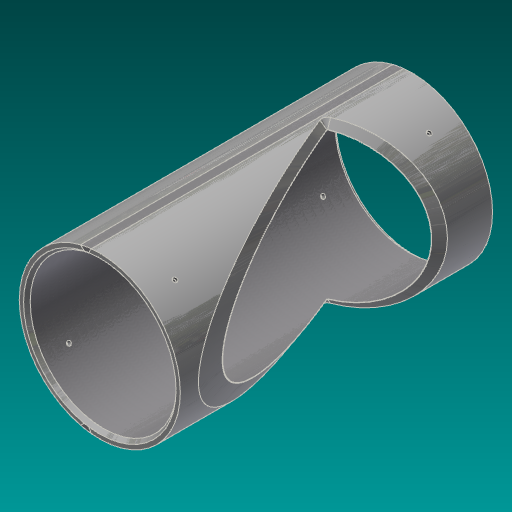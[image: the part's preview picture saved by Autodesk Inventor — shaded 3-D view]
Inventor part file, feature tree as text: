
AUTODESK INVENTOR PART (.ipt)
format: ipt  version: 2017.3 (Build 213256000, 256)  size: 478,208 bytes
history: native  units: in
note: dims shown in document units (in); Inventor stores cm internally (conversion verified against a paired STEP export)
features: other x14, extrude x8, split x8, plane x7, sketch x5, loft x4, chamfer x2, hole x2, pattern_circular x1
ambient origin geometry x8: Origin, YZ Plane, XZ Plane, XY Plane, X Axis, Y Axis, Z Axis, Center Point
bodies: Solid1 (feature_tree)
feature tree (51):
  sketch  "Sketch1"  dims[d0=30.25in d1=33.25in]
  extrude  "Extrusion1"  Depth=33.25in
  sketch  "Sketch2"  dims[d2=47.0236in d3=17.4961in d4=0.0in d5=0.0in d6=22.5deg]
  extrude  "Extrusion2"  TaperAngle=22.5deg  [1 undecoded]
  split  "Split1"
  split  "Split2"
  plane  "Work Plane1"
  plane  "Work Plane2"
  split  "Split3"
  split  "Split4"
  loft  "Loft1"
  loft  "Loft2"
  loft  "Loft3"
  loft  "Loft4"
  chamfer  "Chamfer1"  Angle=90.0deg  [1 undecoded]
  chamfer  "Chamfer2"  Angle=90.0deg  [1 undecoded]
  sketch  "Sketch3"  dims[d7=0.0938in d8=70.0in d9=0.0in]
  plane  "Work Plane3"
  plane  "Work Plane4"
  plane  "Work Plane5"
  plane  "Work Plane6"
  plane  "Work Plane7"
  hole  "Hole1"  [1 undecoded]
  hole  "Hole2"  [1 undecoded]
  pattern_circular  "Circular Pattern1"  Angle=90.0deg  [1 undecoded]
  split  "Split5"
  split  "Split6"
  split  "Split7"
  split  "Split8"
  other  "Srf1"
  other  "Srf2"
  other  "Edges1"
  other  "Edges2"
  other  "Edges3"
  other  "Edges4"
  other  "Edges5"
  other  "Edges6"
  other  "Edges7"
  other  "Edges8"
  sketch  "Sketch4"  dims[d10=30.375in d11=0.0in d12=0.0in]
  sketch  "Sketch5"  dims[d13=1.103in d14=70.0in d15=0.0in d16=22.5deg d17=22.5deg d18=0.0in d19=90.0deg d20=0.0in d21=90.0deg d22=0.0in d23=90.0deg d24=0.0in d25=90.0deg d26=0.0in d27=90.0deg d28=0.0in d29=90.0deg d30=0.0in d31=90.0deg d32=0.0in d33=90.0deg d34=0.75in d35=0.125in d36=0.2749in d37=0.75in d38=0.125in d39=0.2749in d40=75.0deg d41=0.0938in d42=0.0469in d43=0.0687in d46=0.0687in d47=135.0deg d48=-0.9276in d49=6.0in d50=6.0in d51=0.891in d52=0.553in d53=0.0246in d54=0.897in d55=0.375in d56=0.25in d57=0.5635in d58=3.0in d59=0.8108in d60=6.0in d61=6.0in d62=0.891in d63=0.553in d64=0.0246in d65=0.897in d66=0.375in d67=0.25in d68=0.5635in d69=3.0in d70=0.8108in d71=0.7874in d72=1.0994in d74=0.0in d75=0.0in d76=0.0in d77=0.0in]
  other  "Srf3"
  other  "Srf4"
  other  "Srf5"
  other  "Srf6"
  extrude  "ExtrusionSrf1"  TaperAngle=0.0deg  [1 undecoded]
  extrude  "ExtrusionSrf2"  TaperAngle=0.0deg  [1 undecoded]
  extrude  "ExtrusionSrf3"  TaperAngle=0.0deg  [1 undecoded]
  extrude  "ExtrusionSrf4"  Depth=0.0938in
  extrude  "ExtrusionSrf5"  Depth=0.0938in
  extrude  "ExtrusionSrf6"  TaperAngle=75.0deg  [1 undecoded]
note: 10 required parameter values undecoded (feature->parameter linkage not recoverable at this tier; creation-order binding heuristic only, values carry confidence <= 0.55)
